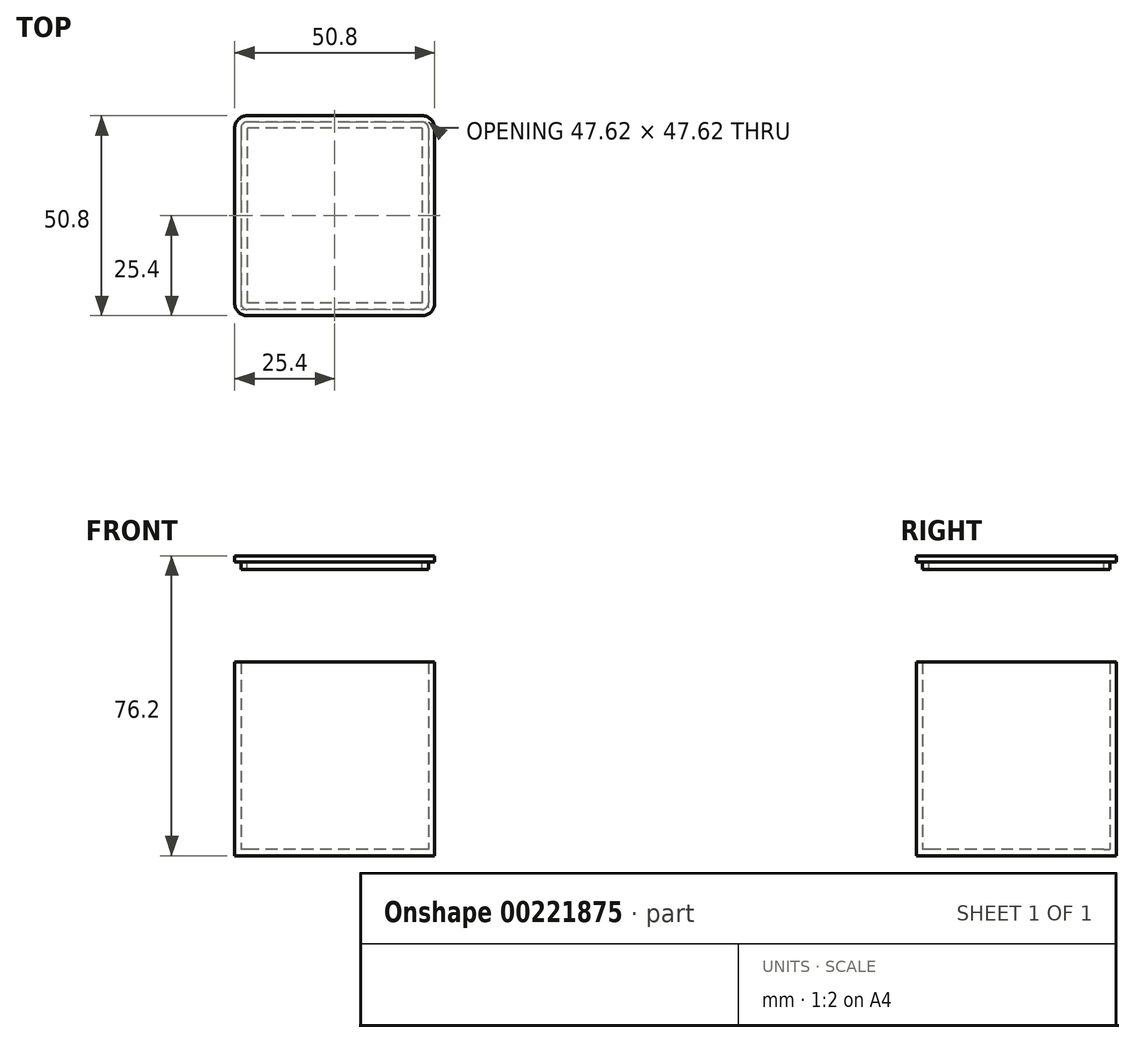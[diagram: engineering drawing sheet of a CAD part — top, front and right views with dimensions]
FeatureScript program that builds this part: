
annotation { "Feature Type Name" : "Feature", "Feature Type Description" : "" }
export const myFeature = defineFeature(function(context is Context, id is Id, definition is map)
    precondition{}
    {
        {
            var Q0;
            Q0=qCreatedBy(makeId("Top.planeOp"),FACE);
            var sketch = newSketch(context, id + "F0", { "sketchPlane" : qUnion([Q0])});
            skLineSegment(sketch, "E0.bottom", {"start": v(22.22, 25.4) * mm, "end": v(-22.23, 25.4) * mm});
            skLineSegment(sketch, "E0.top", {"start": v(22.23, -25.4) * mm, "end": v(-22.23, -25.4) * mm});
            skLineSegment(sketch, "E0.left", {"start": v(25.4, 22.23) * mm, "end": v(25.4, -22.23) * mm});
            skLineSegment(sketch, "E0.right", {"start": v(-25.4, 22.22) * mm, "end": v(-25.4, -22.23) * mm});
            skPoint(sketch, "E0.middle", {"position": v(0, 0) * mm});
            skPoint(sketch, "E1.visualSharp", {"position": v(-25.4, 25.4) * mm});
            skArc(sketch, "E1.filletArc", {"start": v(-22.23, 25.4) * mm, "mid": v(-24.47, 24.47) * mm, "end": v(-25.4, 22.22) * mm});
            skPoint(sketch, "E2.visualSharp", {"position": v(25.4, 25.4) * mm});
            skArc(sketch, "E2.filletArc", {"start": v(25.4, 22.23) * mm, "mid": v(24.47, 24.47) * mm, "end": v(22.22, 25.4) * mm});
            skPoint(sketch, "E3.visualSharp", {"position": v(25.4, -25.4) * mm});
            skArc(sketch, "E3.filletArc", {"start": v(22.23, -25.4) * mm, "mid": v(24.47, -24.47) * mm, "end": v(25.4, -22.23) * mm});
            skPoint(sketch, "E4.visualSharp", {"position": v(-25.4, -25.4) * mm});
            skArc(sketch, "E4.filletArc", {"start": v(-25.4, -22.23) * mm, "mid": v(-24.47, -24.47) * mm, "end": v(-22.23, -25.4) * mm});
            skSolve(sketch);
        }
        {
            var Q0;
            Q0 = qSketchRegion(id + "F0", true);
            extrude(context, id + "F1", {"entities" : qUnion([Q0]), "depth" : 49.2 * mm});
        }
        {
            var Q0;
            Q0=makeQuery(id+"F1.opExtrude","CAP_FACE",FACE,{"disambiguationData":[OSD([sQuery(id+"F0.wireOp",EDGE,"E0.bottom"),sQuery(id+"F0.wireOp",EDGE,"E0.top"),sQuery(id+"F0.wireOp",EDGE,"E0.left"),sQuery(id+"F0.wireOp",EDGE,"E0.right")])],"isStart":false});
            shell(context, id + "F2", {"entities" : qUnion([Q0]), "thickness" : 1.59 * mm});
        }
        {
            var Q0;
            Q0=makeQuery(id+"F1.opExtrude","CAP_FACE",FACE,{"disambiguationData":[OSD([sQuery(id+"F0.wireOp",EDGE,"E0.bottom"),sQuery(id+"F0.wireOp",EDGE,"E0.top"),sQuery(id+"F0.wireOp",EDGE,"E0.left"),sQuery(id+"F0.wireOp",EDGE,"E0.right"),sQuery(id+"F0.wireOp",EDGE,"E1.filletArc"),sQuery(id+"F0.wireOp",EDGE,"E2.filletArc"),sQuery(id+"F0.wireOp",EDGE,"E3.filletArc"),sQuery(id+"F0.wireOp",EDGE,"E4.filletArc")])],"isStart":false});
            cPlane(context, id + "F3", {"entities" : qUnion([Q0]), "cplaneType" : CPlaneType.OFFSET, "offset" : 25.4 * mm, "width" : 152.4 * mm, "height" : 152.4 * mm});
        }
        {
            var Q0;
            Q0=qCreatedBy(id+"F3.planeOp",FACE);
            var sketch = newSketch(context, id + "F4", { "sketchPlane" : qUnion([Q0])});
            skLineSegment(sketch, "E5.0", {"start": v(-25.4, 22.22) * mm, "end": v(-25.4, -22.23) * mm});
            skArc(sketch, "E5.1", {"start": v(-22.23, 25.4) * mm, "mid": v(-24.47, 24.47) * mm, "end": v(-25.4, 22.22) * mm});
            skLineSegment(sketch, "E5.2", {"start": v(22.22, 25.4) * mm, "end": v(-22.23, 25.4) * mm});
            skArc(sketch, "E5.3", {"start": v(25.4, 22.23) * mm, "mid": v(24.47, 24.47) * mm, "end": v(22.22, 25.4) * mm});
            skLineSegment(sketch, "E5.4", {"start": v(25.4, 22.23) * mm, "end": v(25.4, -22.23) * mm});
            skArc(sketch, "E5.5", {"start": v(22.23, -25.4) * mm, "mid": v(24.47, -24.47) * mm, "end": v(25.4, -22.23) * mm});
            skLineSegment(sketch, "E5.6", {"start": v(22.23, -25.4) * mm, "end": v(-22.23, -25.4) * mm});
            skArc(sketch, "E5.7", {"start": v(-25.4, -22.23) * mm, "mid": v(-24.47, -24.47) * mm, "end": v(-22.23, -25.4) * mm});
            skSolve(sketch);
        }
        {
            var Q0;
            Q0 = qSketchRegion(id + "F4", true);
            extrude(context, id + "F5", {"entities" : qUnion([Q0]), "depth" : 1.59 * mm});
        }
        {
            var Q0;
            Q0=makeQuery(id+"F5.opExtrude","CAP_FACE",FACE,{"disambiguationData":[OSD([sQuery(id+"F4.wireOp",EDGE,"E5.0"),sQuery(id+"F4.wireOp",EDGE,"E5.1"),sQuery(id+"F4.wireOp",EDGE,"E5.2"),sQuery(id+"F4.wireOp",EDGE,"E5.3"),sQuery(id+"F4.wireOp",EDGE,"E5.4"),sQuery(id+"F4.wireOp",EDGE,"E5.5"),sQuery(id+"F4.wireOp",EDGE,"E5.6"),sQuery(id+"F4.wireOp",EDGE,"E5.7")])],"isStart":true});
            var sketch = newSketch(context, id + "F6", { "sketchPlane" : qUnion([Q0])});
            skArc(sketch, "E6.0", {"start": v(22.23, 23.81) * mm, "mid": v(23.35, 23.35) * mm, "end": v(23.81, 22.23) * mm});
            skLineSegment(sketch, "E6.1", {"start": v(23.81, -22.23) * mm, "end": v(23.81, 22.23) * mm});
            skLineSegment(sketch, "E6.2", {"start": v(22.23, 23.81) * mm, "end": v(-22.22, 23.81) * mm});
            skArc(sketch, "E6.3", {"start": v(23.81, -22.23) * mm, "mid": v(23.35, -23.35) * mm, "end": v(22.22, -23.81) * mm});
            skArc(sketch, "E6.4", {"start": v(-23.81, 22.23) * mm, "mid": v(-23.35, 23.35) * mm, "end": v(-22.22, 23.81) * mm});
            skLineSegment(sketch, "E6.5", {"start": v(-23.81, -22.22) * mm, "end": v(-23.81, 22.23) * mm});
            skArc(sketch, "E6.6", {"start": v(-22.23, -23.81) * mm, "mid": v(-23.35, -23.35) * mm, "end": v(-23.81, -22.22) * mm});
            skLineSegment(sketch, "E6.7", {"start": v(22.22, -23.81) * mm, "end": v(-22.23, -23.81) * mm});
            skLineSegment(sketch, "E7.0", {"start": v(22.23, 22.23) * mm, "end": v(22.23, 22.23) * mm});
            skLineSegment(sketch, "E7.1", {"start": v(22.23, -22.23) * mm, "end": v(22.23, 22.23) * mm});
            skLineSegment(sketch, "E7.2", {"start": v(22.23, 22.23) * mm, "end": v(-22.22, 22.23) * mm});
            skLineSegment(sketch, "E7.3", {"start": v(22.23, -22.23) * mm, "end": v(22.23, -22.23) * mm});
            skLineSegment(sketch, "E7.4", {"start": v(-22.23, 22.23) * mm, "end": v(-22.23, 22.23) * mm});
            skLineSegment(sketch, "E7.5", {"start": v(-22.23, -22.22) * mm, "end": v(-22.23, 22.23) * mm});
            skLineSegment(sketch, "E7.6", {"start": v(-22.23, -22.23) * mm, "end": v(-22.23, -22.23) * mm});
            skLineSegment(sketch, "E7.7", {"start": v(22.22, -22.23) * mm, "end": v(-22.23, -22.23) * mm});
            skSolve(sketch);
        }
        {
            var Q0;
            Q0 = qSketchRegion(id + "F6", true);
            extrude(context, id + "F7", {"entities" : qUnion([Q0]), "operationType" : NewBodyOperationType.ADD, "depth" : 1.9 * mm});
        }
    });
